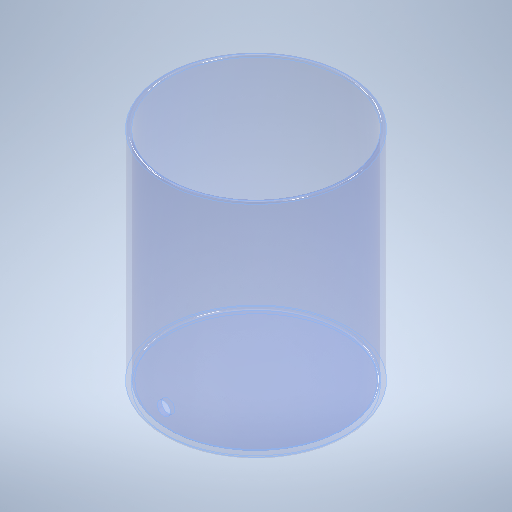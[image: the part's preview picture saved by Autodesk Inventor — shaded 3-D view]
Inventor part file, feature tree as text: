
AUTODESK INVENTOR PART (.ipt)
format: ipt  version: 2025.2 (Build 292293000, 293)  size: 301,056 bytes
history: native  units: mm
features: extrude x3, fillet x3, sketch x3
ambient origin geometry x8: Origin, YZ Plane, XZ Plane, XY Plane, X Axis, Y Axis, Z Axis, Center Point
bodies: Solid1 (feature_tree)
feature tree (9):
  extrude  "Extrusion1"  Depth=2.0mm TaperAngle=0.0deg
  extrude  "Extrusion2"  Depth=1.0mm TaperAngle=0.0deg
  fillet  "Fillet1"  Radius=84.0mm
  fillet  "Fillet2"  Radius=2.0mm
  fillet  "Fillet3"  Radius=1.0mm
  extrude  "Extrusion3"  Depth=10.0mm
  sketch  "Sketch1"  dims[d0=84.0mm d1=2.0mm d2=0.0mm]
  sketch  "Sketch2"  dims[d3=80.0mm d4=100.0mm d5=0.0mm d6=84.0mm d7=2.0mm d8=1.0mm]
  sketch  "Sketch3"  dims[d9=1.0mm d10=10.0mm d11=6.0mm d12=0.0mm d13=0.0mm]
